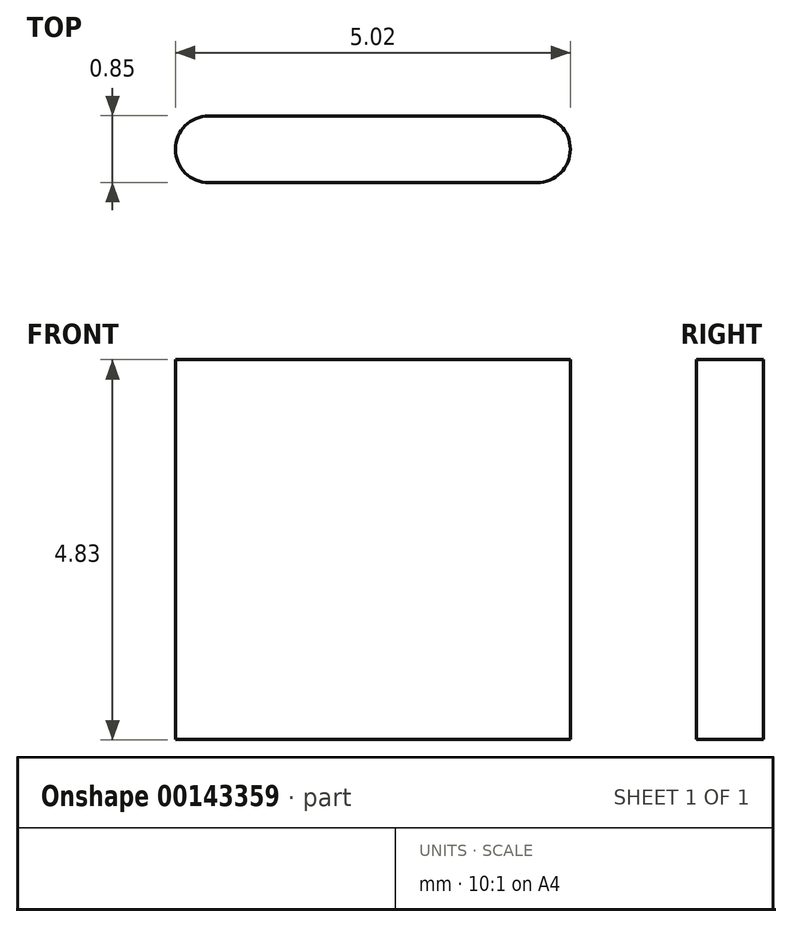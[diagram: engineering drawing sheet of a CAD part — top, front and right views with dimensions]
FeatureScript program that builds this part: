
annotation { "Feature Type Name" : "Feature", "Feature Type Description" : "" }
export const myFeature = defineFeature(function(context is Context, id is Id, definition is map)
    precondition{}
    {
        {
            var Q0;
            Q0=qCreatedBy(makeId("Top.planeOp"),FACE);
            var sketch = newSketch(context, id + "F0", { "sketchPlane" : qUnion([Q0])});
            skLineSegment(sketch, "E0.bottom", {"start": v(-15.24, 16.51) * mm, "end": v(15.24, 16.51) * mm});
            skLineSegment(sketch, "E0.top", {"start": v(-15.24, -16.51) * mm, "end": v(15.24, -16.51) * mm});
            skLineSegment(sketch, "E0.left", {"start": v(-15.24, 16.51) * mm, "end": v(-15.24, -16.51) * mm});
            skLineSegment(sketch, "E0.right", {"start": v(15.24, 16.51) * mm, "end": v(15.24, -16.51) * mm});
            skPoint(sketch, "E0.middle", {"position": v(0, 0) * mm});
            skSolve(sketch);
        }
        {
            var Q0;
            Q0=makeQuery(id+"F0.imprint","IMPRINT",FACE,{"disambiguationData":[TD([[makeQuery(id+"F0.imprint","IMPRINT",EDGE,{"derivedFrom":sQuery(id+"F0.wireOp",EDGE,"E0.bottom")}),-1.0]])]});
            extrude(context, id + "F1", {"entities" : qUnion([Q0]), "oppositeDirection" : true, "depth" : 4.83 * mm});
        }
        {
            var Q0;
            Q0=makeQuery(id+"F1.opExtrude","CAP_FACE",FACE,{"disambiguationData":[OSD([sQuery(id+"F0.wireOp",EDGE,"E0.bottom"),sQuery(id+"F0.wireOp",EDGE,"E0.top"),sQuery(id+"F0.wireOp",EDGE,"E0.left"),sQuery(id+"F0.wireOp",EDGE,"E0.right")])],"isStart":true});
            var sketch = newSketch(context, id + "F2", { "sketchPlane" : qUnion([Q0])});
            skCircle(sketch, "E1", {"center": v(-12.98, 14.24) * mm, "radius": 2.04 * mm});
            skCircle(sketch, "E2.2.0.0", {"center": v(39.22, 14.04) * mm, "radius": 2.25 * mm});
            skCircle(sketch, "E3.2.0.0", {"center": v(37.12, 14.04) * mm, "radius": 1.97 * mm});
            skCircle(sketch, "E3.3.0.0", {"center": v(62.12, 14.04) * mm, "radius": 1.97 * mm});
            skCircle(sketch, "E4.0.1.0", {"center": v(-12.98, -14.35) * mm, "radius": 2.04 * mm});
            skCircle(sketch, "E4.1.0.0", {"center": v(12.92, 14.24) * mm, "radius": 2.04 * mm});
            skCircle(sketch, "E4.1.1.0", {"center": v(12.92, -14.35) * mm, "radius": 2.04 * mm});
            skCircle(sketch, "E4.2.0.0", {"center": v(38.82, 14.24) * mm, "radius": 2.04 * mm});
            skCircle(sketch, "E4.2.1.0", {"center": v(38.82, -14.35) * mm, "radius": 2.04 * mm});
            skLineSegment(sketch, "E4.direction1", {"start": v(-12.98, 14.24) * mm, "end": v(12.92, 14.24) * mm, "construction": true});
            skLineSegment(sketch, "E4.direction2", {"start": v(-12.98, 14.24) * mm, "end": v(-12.98, -14.35) * mm, "construction": true});
            skSolve(sketch);
        }
        {
            var Q0;
            Q0=makeQuery(id+"F2.imprint","IMPRINT",FACE,{"disambiguationData":[TD([[makeQuery(id+"F2.imprint","IMPRINT",EDGE,{"derivedFrom":sQuery(id+"F2.wireOp",EDGE,"E1")}),1.0]])]});
            var Q1;
            Q1=makeQuery(id+"F2.imprint","IMPRINT",FACE,{"disambiguationData":[TD([[makeQuery(id+"F2.imprint","IMPRINT",EDGE,{"derivedFrom":sQuery(id+"F2.wireOp",EDGE,"E4.1.0.0")}),1.0]])]});
            var Q2;
            Q2=makeQuery(id+"F2.imprint","IMPRINT",FACE,{"disambiguationData":[TD([[makeQuery(id+"F2.imprint","IMPRINT",EDGE,{"derivedFrom":sQuery(id+"F2.wireOp",EDGE,"E4.0.1.0")}),1.0]])]});
            var Q3;
            Q3=makeQuery(id+"F2.imprint","IMPRINT",FACE,{"disambiguationData":[TD([[makeQuery(id+"F2.imprint","IMPRINT",EDGE,{"derivedFrom":sQuery(id+"F2.wireOp",EDGE,"E4.1.1.0")}),1.0]])]});
            var Q4;
            Q4=sQuery(id+"F2.wireOp",EDGE,"E1");
            extrude(context, id + "F3", {"entities" : qUnion([Q0, Q1, Q2, Q3]), "operationType" : NewBodyOperationType.REMOVE, "surfaceEntities" : qUnion([Q4]), "oppositeDirection" : true, "depth" : 9.33 * mm});
        }
        {
            var Q0;
            Q0=makeQuery(id+"F1.opExtrude","CAP_FACE",FACE,{"disambiguationData":[OSD([sQuery(id+"F0.wireOp",EDGE,"E0.bottom"),sQuery(id+"F0.wireOp",EDGE,"E0.top"),sQuery(id+"F0.wireOp",EDGE,"E0.left"),sQuery(id+"F0.wireOp",EDGE,"E0.right")])],"isStart":true});
            var sketch = newSketch(context, id + "F4", { "sketchPlane" : qUnion([Q0])});
            skLineSegment(sketch, "E5.bottom", {"start": v(-14.59, 10.36) * mm, "end": v(-10.42, 10.36) * mm});
            skLineSegment(sketch, "E5.top", {"start": v(-14.59, 9.51) * mm, "end": v(-10.42, 9.51) * mm});
            skArc(sketch, "E6", {"start": v(-10.42, 9.51) * mm, "mid": v(-10, 9.94) * mm, "end": v(-10.42, 10.36) * mm});
            skArc(sketch, "E7", {"start": v(-14.59, 10.36) * mm, "mid": v(-15.01, 9.94) * mm, "end": v(-14.59, 9.51) * mm});
            skLineSegment(sketch, "E8.1.0.0", {"start": v(-14.57, 8.7) * mm, "end": v(-10.4, 8.7) * mm});
            skArc(sketch, "E8.1.0.1", {"start": v(-14.57, 8.7) * mm, "mid": v(-15, 8.28) * mm, "end": v(-14.57, 7.86) * mm});
            skLineSegment(sketch, "E8.1.0.2", {"start": v(-14.57, 7.86) * mm, "end": v(-10.4, 7.86) * mm});
            skArc(sketch, "E8.1.0.3", {"start": v(-10.4, 7.86) * mm, "mid": v(-9.98, 8.28) * mm, "end": v(-10.4, 8.7) * mm});
            skLineSegment(sketch, "E8.2.0.0", {"start": v(-14.56, 7.05) * mm, "end": v(-10.39, 7.05) * mm});
            skArc(sketch, "E8.2.0.1", {"start": v(-14.56, 7.05) * mm, "mid": v(-14.98, 6.62) * mm, "end": v(-14.56, 6.2) * mm});
            skLineSegment(sketch, "E8.2.0.2", {"start": v(-14.56, 6.2) * mm, "end": v(-10.39, 6.2) * mm});
            skArc(sketch, "E8.2.0.3", {"start": v(-10.39, 6.2) * mm, "mid": v(-9.97, 6.62) * mm, "end": v(-10.39, 7.05) * mm});
            skLineSegment(sketch, "E8.3.0.0", {"start": v(-14.54, 5.39) * mm, "end": v(-10.37, 5.39) * mm});
            skArc(sketch, "E8.3.0.1", {"start": v(-14.54, 5.39) * mm, "mid": v(-14.97, 4.96) * mm, "end": v(-14.54, 4.54) * mm});
            skLineSegment(sketch, "E8.3.0.2", {"start": v(-14.54, 4.54) * mm, "end": v(-10.37, 4.54) * mm});
            skArc(sketch, "E8.3.0.3", {"start": v(-10.37, 4.54) * mm, "mid": v(-9.95, 4.96) * mm, "end": v(-10.37, 5.39) * mm});
            skLineSegment(sketch, "E8.4.0.0", {"start": v(-14.53, 3.73) * mm, "end": v(-10.36, 3.73) * mm});
            skArc(sketch, "E8.4.0.1", {"start": v(-14.53, 3.73) * mm, "mid": v(-14.95, 3.3) * mm, "end": v(-14.53, 2.88) * mm});
            skLineSegment(sketch, "E8.4.0.2", {"start": v(-14.53, 2.88) * mm, "end": v(-10.36, 2.88) * mm});
            skArc(sketch, "E8.4.0.3", {"start": v(-10.36, 2.88) * mm, "mid": v(-9.94, 3.3) * mm, "end": v(-10.36, 3.73) * mm});
            skLineSegment(sketch, "E8.5.0.0", {"start": v(-14.51, 2.07) * mm, "end": v(-10.34, 2.07) * mm});
            skArc(sketch, "E8.5.0.1", {"start": v(-14.51, 2.07) * mm, "mid": v(-14.94, 1.65) * mm, "end": v(-14.51, 1.22) * mm});
            skLineSegment(sketch, "E8.5.0.2", {"start": v(-14.51, 1.22) * mm, "end": v(-10.34, 1.22) * mm});
            skArc(sketch, "E8.5.0.3", {"start": v(-10.34, 1.22) * mm, "mid": v(-9.92, 1.65) * mm, "end": v(-10.34, 2.07) * mm});
            skLineSegment(sketch, "E8.6.0.0", {"start": v(-14.5, 0.41) * mm, "end": v(-10.33, 0.41) * mm});
            skArc(sketch, "E8.6.0.1", {"start": v(-14.5, 0.41) * mm, "mid": v(-14.92, -0.01) * mm, "end": v(-14.5, -0.43) * mm});
            skLineSegment(sketch, "E8.6.0.2", {"start": v(-14.5, -0.43) * mm, "end": v(-10.33, -0.43) * mm});
            skArc(sketch, "E8.6.0.3", {"start": v(-10.33, -0.43) * mm, "mid": v(-9.9, -0.01) * mm, "end": v(-10.33, 0.41) * mm});
            skLineSegment(sketch, "E8.7.0.0", {"start": v(-14.48, -1.24) * mm, "end": v(-10.31, -1.24) * mm});
            skArc(sketch, "E8.7.0.1", {"start": v(-14.48, -1.24) * mm, "mid": v(-14.9, -1.67) * mm, "end": v(-14.48, -2.1) * mm});
            skLineSegment(sketch, "E8.7.0.2", {"start": v(-14.48, -2.1) * mm, "end": v(-10.31, -2.1) * mm});
            skArc(sketch, "E8.7.0.3", {"start": v(-10.31, -2.1) * mm, "mid": v(-9.9, -1.67) * mm, "end": v(-10.31, -1.24) * mm});
            skLineSegment(sketch, "E8.8.0.0", {"start": v(-14.47, -2.9) * mm, "end": v(-10.3, -2.9) * mm});
            skArc(sketch, "E8.8.0.1", {"start": v(-14.47, -2.9) * mm, "mid": v(-14.9, -3.33) * mm, "end": v(-14.47, -3.75) * mm});
            skLineSegment(sketch, "E8.8.0.2", {"start": v(-14.47, -3.75) * mm, "end": v(-10.3, -3.75) * mm});
            skArc(sketch, "E8.8.0.3", {"start": v(-10.3, -3.75) * mm, "mid": v(-9.88, -3.33) * mm, "end": v(-10.3, -2.9) * mm});
            skLineSegment(sketch, "E8.9.0.0", {"start": v(-14.45, -4.56) * mm, "end": v(-10.29, -4.56) * mm});
            skArc(sketch, "E8.9.0.1", {"start": v(-14.45, -4.56) * mm, "mid": v(-14.88, -4.98) * mm, "end": v(-14.45, -5.4) * mm});
            skLineSegment(sketch, "E8.9.0.2", {"start": v(-14.45, -5.4) * mm, "end": v(-10.29, -5.4) * mm});
            skArc(sketch, "E8.9.0.3", {"start": v(-10.29, -5.4) * mm, "mid": v(-9.86, -4.98) * mm, "end": v(-10.29, -4.56) * mm});
            skLineSegment(sketch, "E8.direction1", {"start": v(-14.59, 10.36) * mm, "end": v(-14.57, 8.7) * mm, "construction": true});
            skLineSegment(sketch, "E9.MirrorCS", {"start": v(14.59, 10.36) * mm, "end": v(10.42, 10.36) * mm});
            skLineSegment(sketch, "E10.MirrorCS", {"start": v(14.59, 9.51) * mm, "end": v(10.42, 9.51) * mm});
            skArc(sketch, "E11.MirrorCS", {"start": v(10.42, 9.51) * mm, "mid": v(10, 9.94) * mm, "end": v(10.42, 10.36) * mm});
            skLineSegment(sketch, "E12.MirrorCS", {"start": v(14.57, 8.7) * mm, "end": v(10.4, 8.7) * mm});
            skArc(sketch, "E13.MirrorCS", {"start": v(14.57, 8.7) * mm, "mid": v(15, 8.28) * mm, "end": v(14.57, 7.86) * mm});
            skLineSegment(sketch, "E14.MirrorCS", {"start": v(14.57, 7.86) * mm, "end": v(10.4, 7.86) * mm});
            skArc(sketch, "E15.MirrorCS", {"start": v(10.4, 7.86) * mm, "mid": v(9.98, 8.28) * mm, "end": v(10.4, 8.7) * mm});
            skLineSegment(sketch, "E16.MirrorCS", {"start": v(14.56, 7.05) * mm, "end": v(10.39, 7.05) * mm});
            skArc(sketch, "E17.MirrorCS", {"start": v(14.56, 7.05) * mm, "mid": v(14.98, 6.62) * mm, "end": v(14.56, 6.2) * mm});
            skLineSegment(sketch, "E18.MirrorCS", {"start": v(14.56, 6.2) * mm, "end": v(10.39, 6.2) * mm});
            skArc(sketch, "E19.MirrorCS", {"start": v(10.39, 6.2) * mm, "mid": v(9.97, 6.62) * mm, "end": v(10.39, 7.05) * mm});
            skArc(sketch, "E20.MirrorCS", {"start": v(14.54, 5.39) * mm, "mid": v(14.97, 4.96) * mm, "end": v(14.54, 4.54) * mm});
            skLineSegment(sketch, "E21.MirrorCS", {"start": v(14.54, 5.39) * mm, "end": v(10.37, 5.39) * mm});
            skArc(sketch, "E22.MirrorCS", {"start": v(10.37, 4.54) * mm, "mid": v(9.95, 4.96) * mm, "end": v(10.37, 5.39) * mm});
            skLineSegment(sketch, "E23.MirrorCS", {"start": v(14.54, 4.54) * mm, "end": v(10.37, 4.54) * mm});
            skLineSegment(sketch, "E24.MirrorCS", {"start": v(14.53, 3.73) * mm, "end": v(10.36, 3.73) * mm});
            skArc(sketch, "E25.MirrorCS", {"start": v(14.53, 3.73) * mm, "mid": v(14.95, 3.3) * mm, "end": v(14.53, 2.88) * mm});
            skLineSegment(sketch, "E26.MirrorCS", {"start": v(14.53, 2.88) * mm, "end": v(10.36, 2.88) * mm});
            skArc(sketch, "E27.MirrorCS", {"start": v(10.36, 2.88) * mm, "mid": v(9.94, 3.3) * mm, "end": v(10.36, 3.73) * mm});
            skLineSegment(sketch, "E28.MirrorCS", {"start": v(14.51, 2.07) * mm, "end": v(10.34, 2.07) * mm});
            skArc(sketch, "E29.MirrorCS", {"start": v(14.51, 2.07) * mm, "mid": v(14.94, 1.65) * mm, "end": v(14.51, 1.22) * mm});
            skLineSegment(sketch, "E30.MirrorCS", {"start": v(14.51, 1.22) * mm, "end": v(10.34, 1.22) * mm});
            skArc(sketch, "E31.MirrorCS", {"start": v(10.34, 1.22) * mm, "mid": v(9.92, 1.65) * mm, "end": v(10.34, 2.07) * mm});
            skLineSegment(sketch, "E32.MirrorCS", {"start": v(14.5, 0.41) * mm, "end": v(10.33, 0.41) * mm});
            skArc(sketch, "E33.MirrorCS", {"start": v(14.5, 0.41) * mm, "mid": v(14.92, -0.01) * mm, "end": v(14.5, -0.43) * mm});
            skLineSegment(sketch, "E34.MirrorCS", {"start": v(14.5, -0.43) * mm, "end": v(10.33, -0.43) * mm});
            skArc(sketch, "E35.MirrorCS", {"start": v(10.33, -0.43) * mm, "mid": v(9.9, -0.01) * mm, "end": v(10.33, 0.41) * mm});
            skLineSegment(sketch, "E36.MirrorCS", {"start": v(14.48, -1.24) * mm, "end": v(10.31, -1.24) * mm});
            skArc(sketch, "E37.MirrorCS", {"start": v(14.48, -1.24) * mm, "mid": v(14.9, -1.67) * mm, "end": v(14.48, -2.1) * mm});
            skLineSegment(sketch, "E38.MirrorCS", {"start": v(14.48, -2.1) * mm, "end": v(10.31, -2.1) * mm});
            skArc(sketch, "E39.MirrorCS", {"start": v(10.31, -2.1) * mm, "mid": v(9.9, -1.67) * mm, "end": v(10.31, -1.24) * mm});
            skLineSegment(sketch, "E40.MirrorCS", {"start": v(14.47, -2.9) * mm, "end": v(10.3, -2.9) * mm});
            skArc(sketch, "E41.MirrorCS", {"start": v(14.47, -2.9) * mm, "mid": v(14.9, -3.33) * mm, "end": v(14.47, -3.75) * mm});
            skLineSegment(sketch, "E42.MirrorCS", {"start": v(14.47, -3.75) * mm, "end": v(10.3, -3.75) * mm});
            skArc(sketch, "E43.MirrorCS", {"start": v(10.3, -3.75) * mm, "mid": v(9.88, -3.33) * mm, "end": v(10.3, -2.9) * mm});
            skLineSegment(sketch, "E44.MirrorCS", {"start": v(14.45, -4.56) * mm, "end": v(10.29, -4.56) * mm});
            skArc(sketch, "E45.MirrorCS", {"start": v(14.45, -4.56) * mm, "mid": v(14.88, -4.98) * mm, "end": v(14.45, -5.4) * mm});
            skLineSegment(sketch, "E46.MirrorCS", {"start": v(14.45, -5.4) * mm, "end": v(10.29, -5.4) * mm});
            skArc(sketch, "E47.MirrorCS", {"start": v(10.29, -5.4) * mm, "mid": v(9.86, -4.98) * mm, "end": v(10.29, -4.56) * mm});
            skArc(sketch, "E48.MirrorCS", {"start": v(14.59, 10.36) * mm, "mid": v(15.01, 9.94) * mm, "end": v(14.59, 9.51) * mm});
            skSolve(sketch);
        }
        {
            var Q0;
            Q0=makeQuery(id+"F4.imprint","IMPRINT",FACE,{"disambiguationData":[TD([[makeQuery(id+"F4.imprint","IMPRINT",EDGE,{"derivedFrom":sQuery(id+"F4.wireOp",EDGE,"E5.bottom")}),-1.0]])]});
            var Q1;
            Q1=makeQuery(id+"F4.imprint","IMPRINT",FACE,{"disambiguationData":[TD([[makeQuery(id+"F4.imprint","IMPRINT",EDGE,{"derivedFrom":sQuery(id+"F4.wireOp",EDGE,"E8.1.0.0")}),-1.0]])]});
            var Q2;
            Q2=makeQuery(id+"F4.imprint","IMPRINT",FACE,{"disambiguationData":[TD([[makeQuery(id+"F4.imprint","IMPRINT",EDGE,{"derivedFrom":sQuery(id+"F4.wireOp",EDGE,"E8.2.0.0")}),-1.0]])]});
            var Q3;
            Q3=makeQuery(id+"F4.imprint","IMPRINT",FACE,{"disambiguationData":[TD([[makeQuery(id+"F4.imprint","IMPRINT",EDGE,{"derivedFrom":sQuery(id+"F4.wireOp",EDGE,"E8.3.0.0")}),-1.0]])]});
            var Q4;
            Q4=makeQuery(id+"F4.imprint","IMPRINT",FACE,{"disambiguationData":[TD([[makeQuery(id+"F4.imprint","IMPRINT",EDGE,{"derivedFrom":sQuery(id+"F4.wireOp",EDGE,"E8.4.0.0")}),-1.0]])]});
            var Q5;
            Q5=makeQuery(id+"F4.imprint","IMPRINT",FACE,{"disambiguationData":[TD([[makeQuery(id+"F4.imprint","IMPRINT",EDGE,{"derivedFrom":sQuery(id+"F4.wireOp",EDGE,"E8.5.0.0")}),-1.0]])]});
            var Q6;
            Q6=makeQuery(id+"F4.imprint","IMPRINT",FACE,{"disambiguationData":[TD([[makeQuery(id+"F4.imprint","IMPRINT",EDGE,{"derivedFrom":sQuery(id+"F4.wireOp",EDGE,"E8.6.0.0")}),-1.0]])]});
            var Q7;
            Q7=makeQuery(id+"F4.imprint","IMPRINT",FACE,{"disambiguationData":[TD([[makeQuery(id+"F4.imprint","IMPRINT",EDGE,{"derivedFrom":sQuery(id+"F4.wireOp",EDGE,"E8.7.0.0")}),-1.0]])]});
            var Q8;
            Q8=makeQuery(id+"F4.imprint","IMPRINT",FACE,{"disambiguationData":[TD([[makeQuery(id+"F4.imprint","IMPRINT",EDGE,{"derivedFrom":sQuery(id+"F4.wireOp",EDGE,"E8.8.0.0")}),-1.0]])]});
            var Q9;
            Q9=makeQuery(id+"F4.imprint","IMPRINT",FACE,{"disambiguationData":[TD([[makeQuery(id+"F4.imprint","IMPRINT",EDGE,{"derivedFrom":sQuery(id+"F4.wireOp",EDGE,"E8.9.0.0")}),-1.0]])]});
            var Q10;
            Q10=makeQuery(id+"F4.imprint","IMPRINT",FACE,{"disambiguationData":[TD([[makeQuery(id+"F4.imprint","IMPRINT",EDGE,{"derivedFrom":sQuery(id+"F4.wireOp",EDGE,"E9.MirrorCS")}),1.0]])]});
            var Q11;
            Q11=makeQuery(id+"F4.imprint","IMPRINT",FACE,{"disambiguationData":[TD([[makeQuery(id+"F4.imprint","IMPRINT",EDGE,{"derivedFrom":sQuery(id+"F4.wireOp",EDGE,"E12.MirrorCS")}),1.0]])]});
            var Q12;
            Q12=makeQuery(id+"F4.imprint","IMPRINT",FACE,{"disambiguationData":[TD([[makeQuery(id+"F4.imprint","IMPRINT",EDGE,{"derivedFrom":sQuery(id+"F4.wireOp",EDGE,"E16.MirrorCS")}),1.0]])]});
            var Q13;
            Q13=makeQuery(id+"F4.imprint","IMPRINT",FACE,{"disambiguationData":[TD([[makeQuery(id+"F4.imprint","IMPRINT",EDGE,{"derivedFrom":sQuery(id+"F4.wireOp",EDGE,"E20.MirrorCS")}),-1.0]])]});
            var Q14;
            Q14=makeQuery(id+"F4.imprint","IMPRINT",FACE,{"disambiguationData":[TD([[makeQuery(id+"F4.imprint","IMPRINT",EDGE,{"derivedFrom":sQuery(id+"F4.wireOp",EDGE,"E24.MirrorCS")}),1.0]])]});
            var Q15;
            Q15=makeQuery(id+"F4.imprint","IMPRINT",FACE,{"disambiguationData":[TD([[makeQuery(id+"F4.imprint","IMPRINT",EDGE,{"derivedFrom":sQuery(id+"F4.wireOp",EDGE,"E28.MirrorCS")}),1.0]])]});
            var Q16;
            Q16=makeQuery(id+"F4.imprint","IMPRINT",FACE,{"disambiguationData":[TD([[makeQuery(id+"F4.imprint","IMPRINT",EDGE,{"derivedFrom":sQuery(id+"F4.wireOp",EDGE,"E32.MirrorCS")}),1.0]])]});
            var Q17;
            Q17=makeQuery(id+"F4.imprint","IMPRINT",FACE,{"disambiguationData":[TD([[makeQuery(id+"F4.imprint","IMPRINT",EDGE,{"derivedFrom":sQuery(id+"F4.wireOp",EDGE,"E36.MirrorCS")}),1.0]])]});
            var Q18;
            Q18=makeQuery(id+"F4.imprint","IMPRINT",FACE,{"disambiguationData":[TD([[makeQuery(id+"F4.imprint","IMPRINT",EDGE,{"derivedFrom":sQuery(id+"F4.wireOp",EDGE,"E40.MirrorCS")}),1.0]])]});
            var Q19;
            Q19=makeQuery(id+"F4.imprint","IMPRINT",FACE,{"disambiguationData":[TD([[makeQuery(id+"F4.imprint","IMPRINT",EDGE,{"derivedFrom":sQuery(id+"F4.wireOp",EDGE,"E44.MirrorCS")}),1.0]])]});
            extrude(context, id + "F5", {"entities" : qUnion([Q0, Q1, Q2, Q3, Q4, Q5, Q6, Q7, Q8, Q9, Q10, Q11, Q12, Q13, Q14, Q15, Q16, Q17, Q18, Q19]), "operationType" : NewBodyOperationType.REMOVE, "oppositeDirection" : true, "depth" : 25 * mm});
        }
    });
